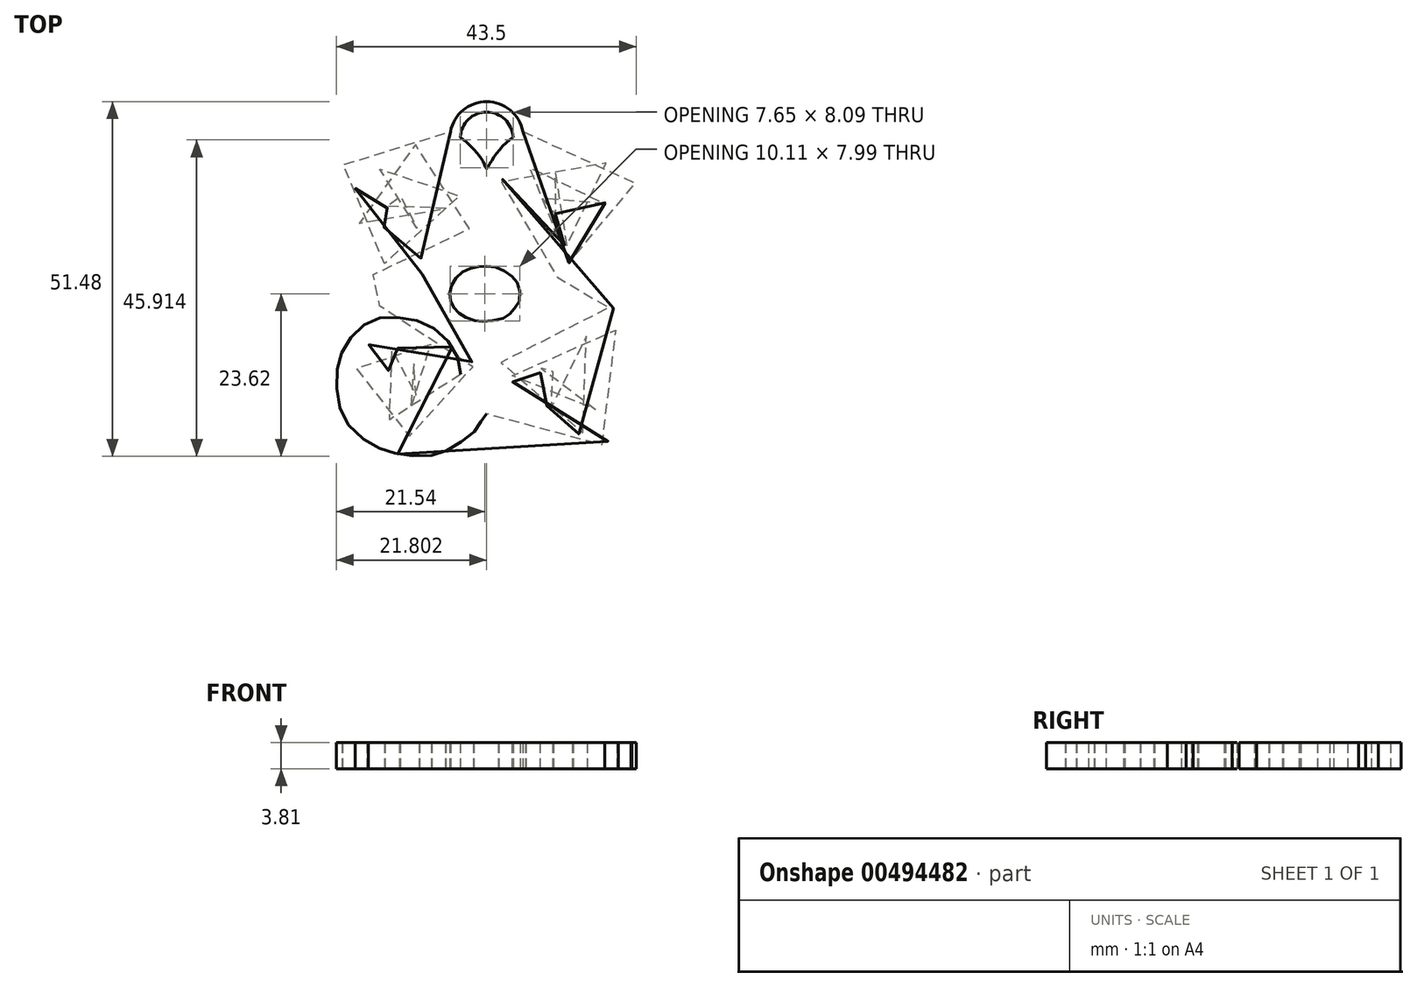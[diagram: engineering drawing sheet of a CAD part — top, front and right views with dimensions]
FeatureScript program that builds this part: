
annotation { "Feature Type Name" : "Feature", "Feature Type Description" : "" }
export const myFeature = defineFeature(function(context is Context, id is Id, definition is map)
    precondition{}
    {
        {
            var Q0;
            Q0=qCreatedBy(makeId("Top.planeOp"),FACE);
            var sketch = newSketch(context, id + "F0", { "sketchPlane" : qUnion([Q0])});
            skPoint(sketch, "E0.middle", {"position": v(0, 0) * mm});
            skFitSpline(sketch, "E1", {"points": [v(0, 1.16) * mm, v(2.1, 0.72) * mm, v(3.73, -0.4) * mm, v(4.66, -1.84) * mm, v(4.66, -4.08) * mm, v(3.66, -5.39) * mm, v(2.73, -6.32) * mm, v(0, -6.82) * mm, v(-1.7, -6.76) * mm, v(-3.5, -6.01) * mm, v(-4.69, -5.01) * mm, v(-5.25, -3.9) * mm, v(-5.3, -2.46) * mm, v(-4.69, -0.96) * mm, v(-3.25, 0.47) * mm, v(-1.7, 0.97) * mm, v(0, 1.16) * mm]});
            skFitSpline(sketch, "E2", {"points": [v(-20.6, 0.63) * mm, v(-16.28, -0.09) * mm, v(-11.05, -0.33) * mm, v(-7.73, 0.5) * mm, v(-5.43, 2.14) * mm, v(-3.25, 4.98) * mm, v(-2.2, 7.64) * mm, v(-1.8, 11.44) * mm, v(-3.25, 15.52) * mm, v(-6.55, 18.24) * mm, v(-9.95, 18.78) * mm, v(-13.62, 18.37) * mm, v(-17.56, 16.2) * mm, v(-18.92, 13.35) * mm, v(-19.06, 9.81) * mm, v(-17.97, 6.41) * mm, v(-14.98, 4.1) * mm, v(-10.36, 4.24) * mm, v(-7.1, 6.41) * mm, v(-5.87, 8.45) * mm, v(-6.42, 11.71) * mm, v(-7.78, 13.75) * mm, v(-11.04, 14.7) * mm, v(-13.9, 13.48) * mm, v(-14.7, 11.17) * mm, v(-14.16, 9.13) * mm, v(-12.53, 8.05) * mm, v(-10.77, 8.18) * mm, v(-9.81, 9) * mm, v(-9.81, 10.12) * mm, v(-10.5, 10.5) * mm, v(-11.37, 10.31) * mm, v(-12.18, 10.75) * mm, v(-12.56, 11.87) * mm, v(-11.68, 12.8) * mm, v(-10.25, 12.8) * mm, v(-9.07, 11.93) * mm, v(-8.2, 11) * mm, v(-7.94, 9) * mm, v(-9.13, 7.38) * mm, v(-11.3, 6.14) * mm, v(-13.93, 6.2) * mm, v(-16.17, 8.13) * mm, v(-17.17, 10) * mm, v(-16.98, 12.8) * mm, v(-15.05, 15.67) * mm, v(-12.06, 17.17) * mm, v(-9.2, 17.1) * mm, v(-6.57, 15.73) * mm, v(-4.77, 13.43) * mm, v(-3.96, 11.43) * mm, v(-3.9, 8.25) * mm, v(-5.45, 5.14) * mm, v(-9.13, 2.46) * mm, v(-12.5, 1.59) * mm, v(-16.05, 1.71) * mm, v(-18.91, 3.52) * mm, v(-21.22, 7.2) * mm, v(-21.78, 11.8) * mm, v(-20.84, 15.73) * mm, v(-18.22, 18.97) * mm, v(-13.98, 21.03) * mm, v(-10.43, 21.65) * mm, v(-6.69, 21.21) * mm, v(-3.82, 19.84) * mm, v(-1.83, 18.04) * mm, v(-0.46, 16.17) * mm, v(0, 15.3) * mm, v(0.54, 16.17) * mm, v(2.97, 19.16) * mm, v(5.7, 20.85) * mm, v(9.48, 21.69) * mm, v(14.1, 20.96) * mm, v(17.86, 19.17) * mm, v(20.38, 16.55) * mm, v(21.49, 13.44) * mm, v(21.58, 9.79) * mm, v(20.96, 6.81) * mm, v(19.67, 4.57) * mm, v(17.58, 2.69) * mm, v(14.98, 1.58) * mm, v(11.86, 1.64) * mm, v(8.69, 2.58) * mm, v(6, 4.51) * mm, v(4.2, 7.07) * mm, v(3.76, 10.68) * mm, v(5.07, 13.98) * mm, v(7, 16.1) * mm, v(9.12, 17.16) * mm, v(12.11, 17.16) * mm, v(13.8, 16.41) * mm, v(15.73, 14.92) * mm, v(16.66, 13.3) * mm, v(17.22, 11.12) * mm, v(16.72, 9) * mm, v(15.6, 7.38) * mm, v(13.86, 6.26) * mm, v(11.99, 5.88) * mm, v(9.75, 6.82) * mm, v(8.25, 8.19) * mm, v(7.81, 9.74) * mm, v(8.37, 11.49) * mm, v(10.12, 12.8) * mm, v(11.43, 12.86) * mm, v(12.36, 12.17) * mm, v(12.36, 11.05) * mm, v(11.8, 10.3) * mm, v(11.05, 10.3) * mm, v(10.56, 10.5) * mm, v(9.93, 10.24) * mm, v(9.75, 9.56) * mm, v(10.24, 8.37) * mm, v(11.68, 7.88) * mm, v(13.36, 8.31) * mm, v(14.54, 9.68) * mm, v(14.6, 11.36) * mm, v(14.1, 13.05) * mm, v(12.55, 14.36) * mm, v(11.12, 14.67) * mm, v(9.25, 14.6) * mm, v(7.56, 13.67) * mm, v(6.32, 12.11) * mm, v(5.76, 9.62) * mm, v(6.26, 7.5) * mm, v(8.5, 5.13) * mm, v(10.68, 4.26) * mm, v(13.73, 4.07) * mm, v(16.16, 4.7) * mm, v(17.97, 6.75) * mm, v(18.84, 8.87) * mm, v(18.84, 12.92) * mm, v(18.24, 14.98) * mm, v(15.8, 17.29) * mm, v(12.7, 18.6) * mm, v(10.01, 18.85) * mm, v(7.2, 18.6) * mm, v(4.22, 16.85) * mm, v(2.4, 14.11) * mm, v(1.79, 11.3) * mm, v(1.97, 8.2) * mm, v(2.84, 5.39) * mm, v(5.23, 2.26) * mm, v(7.53, 0.77) * mm, v(9.71, -0.35) * mm, v(14.08, -0.35) * mm, v(20.87, 0.47) * mm, v(20.97, 0.32) * mm, v(20.95, -2.3) * mm, v(21, -5.12) * mm, v(20.73, -5.16) * mm, v(17.4, -4.85) * mm, v(13.16, -4.46) * mm, v(9.6, -4.54) * mm, v(6.4, -6.01) * mm, v(3.9, -8.5) * mm, v(2.29, -11.87) * mm, v(1.85, -15.54) * mm, v(2.35, -18.7) * mm, v(4.03, -21.31) * mm, v(6.86, -23.2) * mm, v(11.68, -23.52) * mm, v(14.82, -22.68) * mm, v(17.65, -20.69) * mm, v(19.01, -17.33) * mm, v(18.8, -13.56) * mm, v(17.55, -10.84) * mm, v(15.66, -9.37) * mm, v(12.52, -8.95) * mm, v(8.95, -9.58) * mm, v(6.54, -11.78) * mm, v(5.7, -14.4) * mm, v(6.54, -17.33) * mm, v(8.64, -19.11) * mm, v(11.47, -19.32) * mm, v(13.46, -18.49) * mm, v(14.61, -16.18) * mm, v(14.4, -14.3) * mm, v(13.14, -13.04) * mm, v(11.15, -12.83) * mm, v(9.9, -13.45) * mm, v(9.69, -14.6) * mm, v(10.84, -15.24) * mm, v(11.89, -15.03) * mm, v(12.62, -16.28) * mm, v(12, -17.44) * mm, v(10.73, -17.75) * mm, v(9.16, -16.91) * mm, v(8.22, -15.97) * mm, v(7.8, -14.19) * mm, v(9.27, -11.99) * mm, v(12.1, -10.84) * mm, v(14.82, -11.46) * mm, v(16.5, -13.35) * mm, v(17.13, -15.87) * mm, v(16.5, -18.6) * mm, v(14.5, -20.8) * mm, v(12.29, -21.78) * mm, v(9.47, -21.93) * mm, v(7.36, -21) * mm, v(5.5, -19.3) * mm, v(4.06, -16.96) * mm, v(3.8, -13.74) * mm, v(5, -10.47) * mm, v(8.57, -7.5) * mm, v(11.72, -6.36) * mm, v(15.44, -6.36) * mm, v(18.59, -8.06) * mm, v(20.69, -11.05) * mm, v(21.58, -14.52) * mm, v(21.55, -18.33) * mm, v(20.5, -21.16) * mm, v(18.32, -23.75) * mm, v(15, -25.44) * mm, v(11.05, -26.33) * mm, v(6.85, -26.17) * mm, v(4.1, -24.8) * mm, v(2.16, -23.26) * mm, v(0, -20.27) * mm, v(-0.53, -20.78) * mm, v(-1.11, -21.9) * mm, v(-2.36, -23.4) * mm, v(-5.05, -25.17) * mm, v(-7.36, -26.18) * mm, v(-11.04, -26.36) * mm, v(-14.06, -25.8) * mm, v(-16.88, -24.61) * mm, v(-20.17, -21.72) * mm, v(-21.56, -18.19) * mm, v(-21.72, -14.15) * mm, v(-20.91, -11.24) * mm, v(-18.98, -8.33) * mm, v(-16.23, -6.55) * mm, v(-12.91, -6.31) * mm, v(-9.12, -7.12) * mm, v(-6.05, -9.22) * mm, v(-4.1, -12.37) * mm, v(-3.84, -15.5) * mm, v(-4.94, -18.6) * mm, v(-6.9, -20.8) * mm, v(-9.55, -21.96) * mm, v(-11.95, -21.91) * mm, v(-14.06, -21.14) * mm, v(-15.84, -19.6) * mm, v(-16.7, -18.07) * mm, v(-17.14, -15.81) * mm, v(-16.8, -13.94) * mm, v(-15.75, -12.3) * mm, v(-14.02, -11.05) * mm, v(-11.76, -10.72) * mm, v(-9.74, -11.63) * mm, v(-8.4, -13.02) * mm, v(-7.96, -14.18) * mm, v(-8.25, -15.76) * mm, v(-9.26, -16.92) * mm, v(-10.41, -17.68) * mm, v(-11.47, -17.68) * mm, v(-12.24, -17.25) * mm, v(-12.48, -16.2) * mm, v(-12.24, -15.33) * mm, v(-11.33, -15.04) * mm, v(-10.56, -15.19) * mm, v(-9.79, -14.9) * mm, v(-9.88, -13.89) * mm, v(-10.85, -12.88) * mm, v(-12.05, -12.74) * mm, v(-13.4, -13.22) * mm, v(-14.5, -14.46) * mm, v(-14.69, -16.43) * mm, v(-14.06, -18.02) * mm, v(-12.14, -19.27) * mm, v(-9.84, -19.41) * mm, v(-8.1, -18.79) * mm, v(-6.62, -17.35) * mm, v(-5.94, -15.23) * mm, v(-6.18, -12.93) * mm, v(-7.2, -11.05) * mm, v(-9.3, -9.49) * mm, v(-11.48, -8.92) * mm, v(-13.99, -8.92) * mm, v(-15.76, -9.32) * mm, v(-17.7, -10.94) * mm, v(-18.75, -13.12) * mm, v(-19.08, -15.63) * mm, v(-18.84, -18.21) * mm, v(-17.78, -20.48) * mm, v(-16, -22.23) * mm, v(-13.5, -23.14) * mm, v(-9.87, -23.63) * mm, v(-7.04, -23.3) * mm, v(-3.97, -21.37) * mm, v(-2.43, -18.62) * mm, v(-1.87, -15.06) * mm, v(-2.67, -11.18) * mm, v(-5.26, -7.06) * mm, v(-8.78, -5.01) * mm, v(-12.44, -4.47) * mm, v(-16.87, -4.83) * mm, v(-20.8, -5.31) * mm, v(-20.87, -5.01) * mm, v(-20.86, 0.16) * mm, v(-20.83, 0.47) * mm, v(-20.78, 0.6) * mm, v(-20.6, 0.63) * mm]});
            skArc(sketch, "E3", {"start": v(3.83, 19.84) * mm, "mid": v(0, 23.5) * mm, "end": v(-3.82, 19.84) * mm});
            skArc(sketch, "E4.0", {"start": v(5.26, 20.66) * mm, "mid": v(0.01, 25.02) * mm, "end": v(-5.26, 20.68) * mm});
            skSolve(sketch);
        }
        {
            var Q0;
            Q0=makeQuery(id+"F0.imprint","IMPRINT",FACE,{"disambiguationData":[TD([[makeQuery(id+"F0.imprint","IMPRINT",EDGE,{"derivedFrom":sQuery(id+"F0.wireOp",EDGE,"E1")}),1.0]])]});
            var Q1;
            {var subQ0=sQuery(id+"F0.wireOp",EDGE,"E3");Q1=makeQuery(id+"F0.imprint","IMPRINT",FACE,{"disambiguationData":[TD([[makeQuery(id+"F0.imprint","IMPRINT",EDGE,{"derivedFrom":subQ0}),-1.0]])]});}
            extrude(context, id + "F1", {"entities" : qUnion([Q0, Q1]), "depth" : 3.8 * mm});
        }
    });
